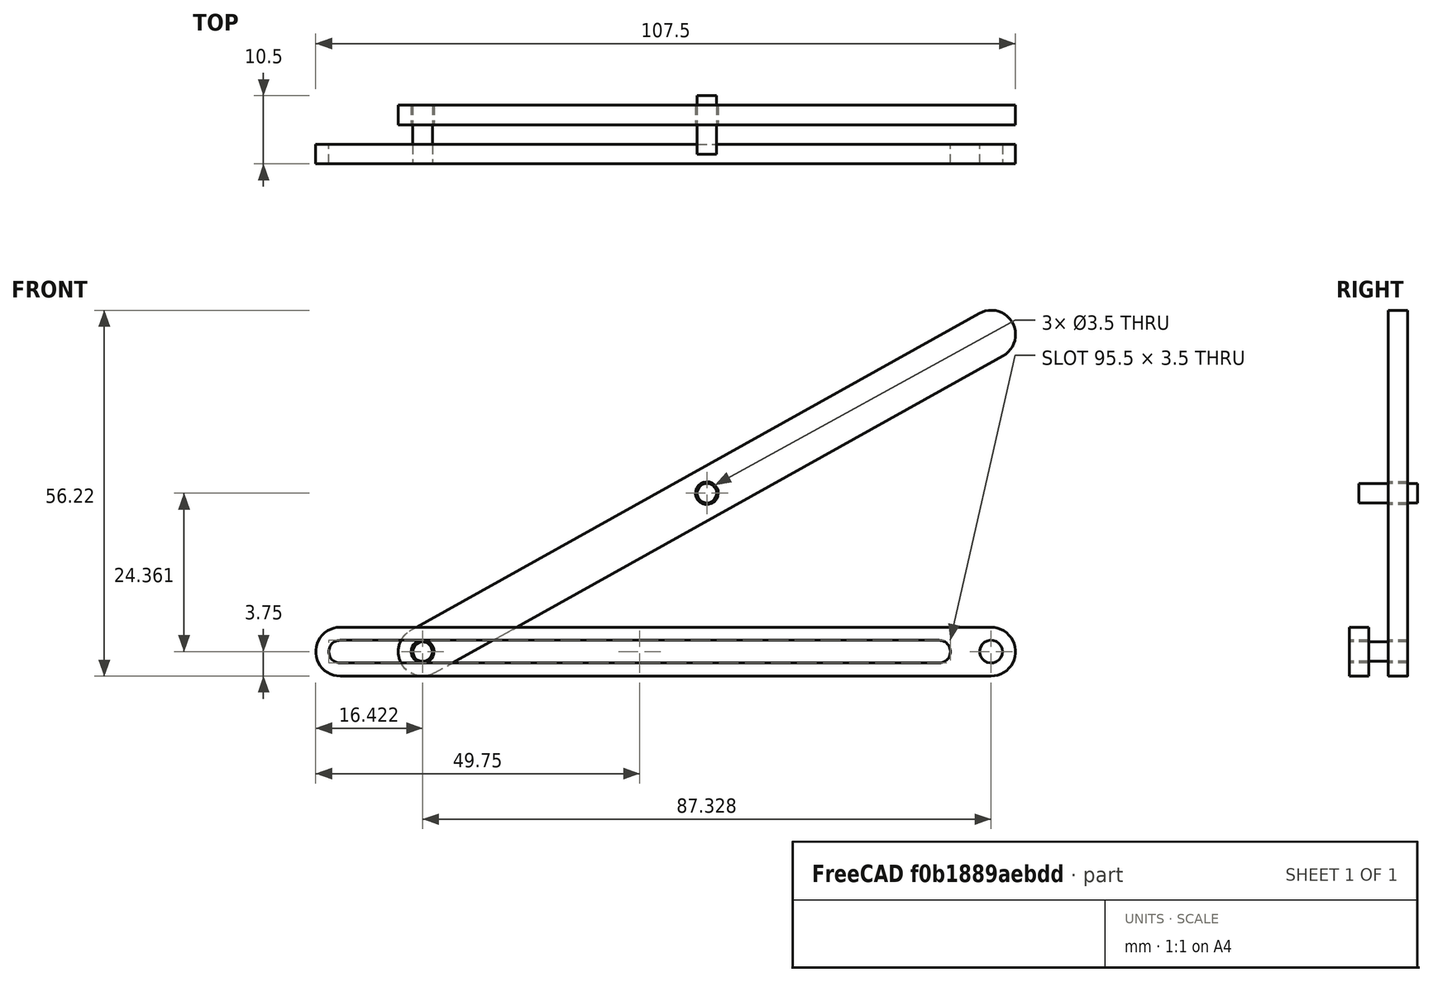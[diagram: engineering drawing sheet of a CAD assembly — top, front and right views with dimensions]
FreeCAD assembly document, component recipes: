
FREECAD ASSEMBLY — COMPONENT RECIPES ("scissor_lift")

This assembly document has 6 components, labeled P0..P5 below (a component is one placed body or linked part). 6 of them carry a construction recipe — the FreeCAD feature program that regenerates the part from scratch, quoted from this document or its linked companion documents; the rest are supplied as boundary geometry only. No exploded tour is included for this assembly.
COMPONENT P0 — recipe-attached ("base", modeled in this document).
Construction recipe (the document's own serialized feature program — sketch geometry with constraints, then the solid features built on it; lengths are millimeters unless a unit is written):

FEATURE [Sketcher::SketchObject] Sketch
  ArcFitTolerance = 1e-06
  AttachmentSupport = -> [XY_Plane]
  FullyConstrained = true
  MakeInternals = false
  MapMode = 5
  sketch-geometry (9):
    g0: ArcOfCircle CenterX=-50 CenterY=0 CenterZ=0 NormalX=0 NormalY=0 NormalZ=1 AngleXU=0 Radius=3.75 StartAngle=1.5708 EndAngle=4.71239
    g1: ArcOfCircle CenterX=50 CenterY=0 CenterZ=0 NormalX=0 NormalY=0 NormalZ=1 AngleXU=0 Radius=3.75 StartAngle=4.71239 EndAngle=7.85398
    g2: LineSegment StartX=-50 StartY=3.75 StartZ=0 EndX=50 EndY=3.75 EndZ=0
    g3: LineSegment StartX=-50 StartY=-3.75 StartZ=0 EndX=50 EndY=-3.75 EndZ=0
    g4: ArcOfCircle CenterX=-50 CenterY=0 CenterZ=0 NormalX=0 NormalY=0 NormalZ=1 AngleXU=0 Radius=1.75 StartAngle=1.5708 EndAngle=4.71239
    g5: ArcOfCircle CenterX=42 CenterY=1.1702e-12 CenterZ=0 NormalX=0 NormalY=0 NormalZ=1 AngleXU=0 Radius=1.75 StartAngle=4.71239 EndAngle=7.85398
    g6: LineSegment StartX=-50 StartY=1.75 StartZ=0 EndX=42 EndY=1.75 EndZ=0
    g7: LineSegment StartX=-50 StartY=-1.75 StartZ=0 EndX=42 EndY=-1.75 EndZ=0
    g8: Circle CenterX=50 CenterY=0 CenterZ=0 NormalX=0 NormalY=0 NormalZ=1 AngleXU=0 Radius=1.75
  constraints (20):
    c: Tangent(g0,g2) = 1.5708
    c: Tangent(g0,g3) = -1.5708
    c: Tangent(g1,g2) = 1.5708
    c: Tangent(g1,g3) = -1.5708
    c: Equal(g0,g1)
    c: PointOnObject(g0,g-1)
    c: Symmetric(g0,g1,g-1)
    c: DistanceX(g0,g1) = 100
    c: DistanceY(g0,g0) = 7.5
    c: Tangent(g4,g6) = 1.5708
    c: Tangent(g4,g7) = -1.5708
    c: Tangent(g5,g6) = 1.5708
    c: Tangent(g5,g7) = -1.5708
    c: Equal(g4,g5)
    c: Horizontal(g7)
    c: Coincident(g4,g0)
    c: Distance(g4,g4) = 3.5
    c: Coincident(g8,g1)
    c: Diameter(g8) = 3.5
    c: DistanceX(g5,g1) = 8
FEATURE [PartDesign::Pad] Pad
  Direction = (0,0,1)
  Length = 3
  Length2 = 10
  Profile = -> Sketch
  ReferenceAxis = -> Sketch [N_Axis]
  Suppressed = false
  Type = 0
FEATURE [PartDesign::Body] Body  label="base"
  AllowCompound = false
  Group = -> [Sketch,Pad]
  Origin = -> Origin
  Placement = pos=(0,1.5,1.5) rot=(1,0,0;1.5708rad)
  Tip = -> Pad
COMPONENT P1 — recipe-attached ("arm_1", modeled in this document).
Construction recipe (the document's own serialized feature program — sketch geometry with constraints, then the solid features built on it; lengths are millimeters unless a unit is written):

FEATURE [PartDesign::SubShapeBinder] Binder
  BindCopyOnChange = 0
  BindMode = 0
  ClaimChildren = false
  Context = -> Body001 [Binder.]
  Fuse = false
  MakeFace = true
  OffsetFill = false
  OffsetIntersection = false
  OffsetJoinType = 0
  OffsetOpenResult = false
  PartialLoad = false
  Relative = true
  Support = -> [Body]
  _Version = 2
FEATURE [Sketcher::SketchObject] Sketch001
  ArcFitTolerance = 1e-06
  AttachmentSupport = -> [XY_Plane001]
  ExternalGeometry = -> [Binder]
  FullyConstrained = true
  MakeInternals = false
  MapMode = 5
  sketch-geometry (6):
    g0: ArcOfCircle CenterX=-50 CenterY=-2e-16 CenterZ=0 NormalX=0 NormalY=0 NormalZ=1 AngleXU=0 Radius=3.75 StartAngle=1.5708 EndAngle=4.71239
    g1: ArcOfCircle CenterX=50 CenterY=2e-16 CenterZ=0 NormalX=0 NormalY=0 NormalZ=1 AngleXU=0 Radius=3.75 StartAngle=4.71239 EndAngle=7.85398
    g2: LineSegment StartX=-50 StartY=3.75 StartZ=0 EndX=50 EndY=3.75 EndZ=0
    g3: LineSegment StartX=-50 StartY=-3.75 StartZ=0 EndX=50 EndY=-3.75 EndZ=0
    g4: Circle CenterX=-50 CenterY=-2e-16 CenterZ=0 NormalX=0 NormalY=0 NormalZ=1 AngleXU=0 Radius=1.75
    g5: Circle CenterX=0 CenterY=0 CenterZ=0 NormalX=0 NormalY=0 NormalZ=1 AngleXU=0 Radius=1.75
  constraints (13):
    c: Tangent(g0,g2) = 1.5708
    c: Tangent(g0,g3) = -1.5708
    c: Tangent(g1,g2) = 1.5708
    c: Tangent(g1,g3) = -1.5708
    c: Equal(g0,g1)
    c: Horizontal(g2)
    c: Symmetric(g0,g1,g-1)
    c: Equal(g-3,g2)
    c: Equal(g-4,g1)
    c: Coincident(g4,g0)
    c: Equal(g4,g-5)
    c: Coincident(g5,g-1)
    c: Equal(g4,g5)
FEATURE [PartDesign::Pad] Pad001
  Direction = (0,0,1)
  Length = 3
  Length2 = 10
  Profile = -> Sketch001
  ReferenceAxis = -> Sketch001 [N_Axis]
  Suppressed = false
  Type = 0
FEATURE [PartDesign::Body] Body001  label="arm_1"
  AllowCompound = false
  Group = -> [Binder,Sketch001,Pad001]
  Origin = -> Origin001
  Placement = pos=(6.33603,1.5,25.861) rot=(0.180877,0.695443,0.695444;3.49948rad)
  Tip = -> Pad001
COMPONENT P2 — recipe-attached ("arm_2", modeled in this document).
Construction recipe (the document's own serialized feature program — sketch geometry with constraints, then the solid features built on it; lengths are millimeters unless a unit is written):

FEATURE [PartDesign::FeatureBase] Clone
  BaseFeature = -> Body001
  Placement = pos=(0,23.6,0) rot=(0,0,1;0rad)
  Suppressed = false
FEATURE [PartDesign::Body] Body002  label="arm_2"
  AllowCompound = false
  Group = -> [Clone]
  Origin = -> Origin002
  Placement = pos=(-5.16236,4.49999,46.4704) rot=(-0.938525,-0.2441,-0.2441;1.6342rad)
  Tip = -> Clone
COMPONENT P3 — recipe-attached ("pin_1", modeled in this document).
Construction recipe (the document's own serialized feature program — sketch geometry with constraints, then the solid features built on it; lengths are millimeters unless a unit is written):

FEATURE [Sketcher::SketchObject] Sketch002
  ArcFitTolerance = 1e-06
  AttachmentSupport = -> [XY_Plane003]
  FullyConstrained = true
  MakeInternals = false
  MapMode = 5
  sketch-geometry (1):
    g0: Circle CenterX=0 CenterY=0 CenterZ=0 NormalX=0 NormalY=0 NormalZ=1 AngleXU=0 Radius=1.5
  constraints (2):
    c: Coincident(g0,g-1)
    c: Diameter(g0) = 3
FEATURE [PartDesign::Pad] Pad002
  Direction = (0,0,1)
  Length = 9
  Length2 = 10
  Profile = -> Sketch002
  ReferenceAxis = -> Sketch002 [N_Axis]
  Suppressed = false
  Type = 0
FEATURE [PartDesign::Body] Body003  label="pin_1"
  AllowCompound = false
  Group = -> [Sketch002,Pad002]
  Origin = -> Origin003
  Placement = pos=(50,7.5,1.5) rot=(0.993796,-0.078645,0.078645;1.57702rad)
  Tip = -> Pad002
COMPONENT P4 — recipe-attached ("pin_2", modeled in this document).
Construction recipe (the document's own serialized feature program — sketch geometry with constraints, then the solid features built on it; lengths are millimeters unless a unit is written):

FEATURE [PartDesign::FeatureBase] Clone001
  BaseFeature = -> Body003
  Placement = pos=(-78.7,0,0) rot=(0,0,1;0rad)
  Suppressed = false
FEATURE [PartDesign::Body] Body004  label="pin_2"
  AllowCompound = false
  Group = -> [Clone001]
  Origin = -> Origin004
  Placement = pos=(-28.489,-1.54373e-05,96.4365) rot=(0.402424,0.647323,0.647323;3.90678rad)
  Tip = -> Clone001
COMPONENT P5 — recipe-attached ("pin_3", modeled in this document).
Construction recipe (the document's own serialized feature program — sketch geometry with constraints, then the solid features built on it; lengths are millimeters unless a unit is written):

FEATURE [PartDesign::FeatureBase] Clone002
  BaseFeature = -> Body003
  Placement = pos=(-78.7,0,0) rot=(0,0,1;0rad)
  Suppressed = false
FEATURE [PartDesign::Body] Body005  label="pin_3"
  AllowCompound = false
  Group = -> [Clone002]
  Origin = -> Origin005
  Placement = pos=(28.0818,-1.50001,45.2637) rot=(-0.918845,-0.279038,-0.279038;1.65533rad)
  Tip = -> Clone002
PROVENANCE & LICENSES
A FreeCAD (.FCStd) document from a public repository crawl; recipes are the document's own serialized feature recipes (and, for linked parts, companion documents' recipes).
License: as declared in the source repository (recorded in the dataset sidecar).
